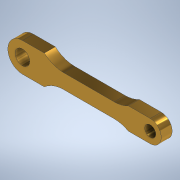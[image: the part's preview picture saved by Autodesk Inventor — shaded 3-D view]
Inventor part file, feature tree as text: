
AUTODESK INVENTOR PART (.ipt)
format: ipt  version: 2022 (Build 260153000, 153)  size: 147,456 bytes
history: native  units: mm
features: fillet x2, extrude x1, sketch x1
ambient origin geometry x8: Origin, YZ Plane, XZ Plane, XY Plane, X Axis, Y Axis, Z Axis, Center Point
bodies: Solid1 (feature_tree)
feature tree (4):
  extrude  "Extrusion1"  Depth=4.0mm
  fillet  "Fillet1"  Radius=6.0mm
  fillet  "Fillet2"  Radius=3.0mm
  sketch  "Sketch1"  dims[d0=8.0mm d1=4.0mm d8=6.0mm d9=3.0mm d10=6.0mm d11=6.0mm d12=6.0mm d13=3.0mm d14=0.0mm d15=8.0mm d16=8.0mm]
